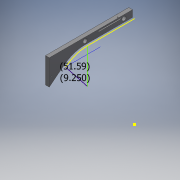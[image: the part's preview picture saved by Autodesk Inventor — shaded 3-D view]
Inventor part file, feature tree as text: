
AUTODESK INVENTOR PART (.ipt)
format: ipt  version: 2018 (Build 220112000, 112)  size: 167,936 bytes
history: native  units: in
note: dims shown in document units (in); Inventor stores cm internally (conversion verified against a paired STEP export)
features: direct_edit x4, move_body x4, other x1, sketch x1
ambient origin geometry x8: Origin, YZ Plane, XZ Plane, XY Plane, X Axis, Y Axis, Z Axis, Center Point
bodies: Solid1 (feature_tree)
feature tree (10):
  other  "RIGHT Bottom Part 1"
  direct_edit  "Direct Edit1"
  sketch  "Sketch2"  dims[d0=0.0in d1=0.0in d2=0.25in d5=9.25in d6=0.3545in d7=0.0in d8=0.0in d9=-0.125in d10=0.0in d11=0.0in d12=-0.375in d13=0.0in d14=0.0in d15=-0.125in]
  direct_edit  "Direct Edit2"
  direct_edit  "Direct Edit3"
  direct_edit  "Direct Edit4"
  move_body  "Move1"
  move_body  "Move2"
  move_body  "Move3"
  move_body  "Move4"
